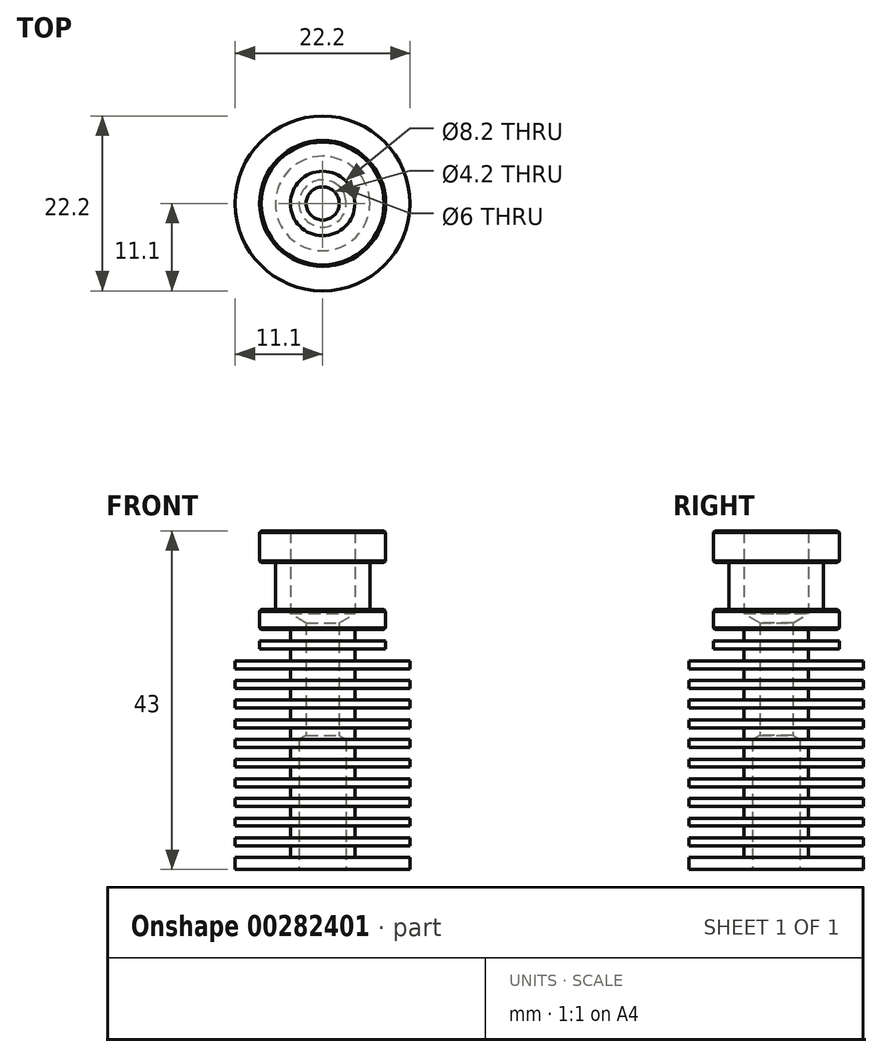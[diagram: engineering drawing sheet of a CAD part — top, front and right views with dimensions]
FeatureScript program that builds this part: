
annotation { "Feature Type Name" : "Feature", "Feature Type Description" : "" }
export const myFeature = defineFeature(function(context is Context, id is Id, definition is map)
    precondition{}
    {
        {
            var Q0;
            Q0=qCreatedBy(makeId("Front.planeOp"),FACE);
            var sketch = newSketch(context, id + "F0", { "sketchPlane" : qUnion([Q0])});
            skLineSegment(sketch, "E0", {"start": v(0, 0) * mm, "end": v(0, 43) * mm, "construction": true});
            skLineSegment(sketch, "E1", {"start": v(4.1, 43) * mm, "end": v(8, 43) * mm});
            skLineSegment(sketch, "E2", {"start": v(8, 43) * mm, "end": v(8, 39) * mm});
            skLineSegment(sketch, "E3", {"start": v(8, 39) * mm, "end": v(6, 39) * mm});
            skLineSegment(sketch, "E4", {"start": v(6, 39) * mm, "end": v(6, 33) * mm});
            skLineSegment(sketch, "E5", {"start": v(6, 33) * mm, "end": v(8, 33) * mm});
            skLineSegment(sketch, "E6", {"start": v(8, 33) * mm, "end": v(8, 30.5) * mm});
            skLineSegment(sketch, "E7", {"start": v(8, 30.5) * mm, "end": v(4.1, 30.5) * mm});
            skLineSegment(sketch, "E8", {"start": v(4.1, 30.5) * mm, "end": v(4.1, 29) * mm});
            skLineSegment(sketch, "E9", {"start": v(4.1, 29) * mm, "end": v(8, 29) * mm});
            skLineSegment(sketch, "E10", {"start": v(8, 29) * mm, "end": v(8, 28) * mm});
            skLineSegment(sketch, "E11", {"start": v(8, 28) * mm, "end": v(4.1, 28) * mm});
            skLineSegment(sketch, "E12", {"start": v(4.1, 28) * mm, "end": v(4.1, 26.5) * mm});
            skLineSegment(sketch, "E13", {"start": v(4.1, 26.5) * mm, "end": v(11.1, 26.5) * mm});
            skLineSegment(sketch, "E14", {"start": v(11.1, 26.5) * mm, "end": v(11.1, 25.5) * mm});
            skLineSegment(sketch, "E15", {"start": v(11.1, 25.5) * mm, "end": v(4.1, 25.5) * mm});
            skLineSegment(sketch, "E16", {"start": v(4.1, 25.5) * mm, "end": v(4.1, 24) * mm});
            skLineSegment(sketch, "E17", {"start": v(4.1, 24) * mm, "end": v(11.1, 24) * mm});
            skLineSegment(sketch, "E18", {"start": v(11.1, 24) * mm, "end": v(11.1, 23) * mm});
            skLineSegment(sketch, "E19", {"start": v(11.1, 23) * mm, "end": v(4.1, 23) * mm});
            skLineSegment(sketch, "E20", {"start": v(4.1, 23) * mm, "end": v(4.1, 21.5) * mm});
            skLineSegment(sketch, "E21", {"start": v(4.1, 21.5) * mm, "end": v(11.1, 21.5) * mm});
            skLineSegment(sketch, "E22", {"start": v(11.1, 21.5) * mm, "end": v(11.1, 20.5) * mm});
            skLineSegment(sketch, "E23", {"start": v(11.1, 20.5) * mm, "end": v(4.1, 20.5) * mm});
            skLineSegment(sketch, "E24", {"start": v(4.1, 20.5) * mm, "end": v(4.1, 19) * mm});
            skLineSegment(sketch, "E25", {"start": v(4.1, 19) * mm, "end": v(11.1, 19) * mm});
            skLineSegment(sketch, "E26", {"start": v(11.1, 19) * mm, "end": v(11.1, 18) * mm});
            skLineSegment(sketch, "E27", {"start": v(11.1, 18) * mm, "end": v(4.1, 18) * mm});
            skLineSegment(sketch, "E28", {"start": v(4.1, 18) * mm, "end": v(4.1, 16.5) * mm});
            skLineSegment(sketch, "E29", {"start": v(4.1, 16.5) * mm, "end": v(11.1, 16.5) * mm});
            skLineSegment(sketch, "E30", {"start": v(11.1, 16.5) * mm, "end": v(11.1, 15.5) * mm});
            skLineSegment(sketch, "E31", {"start": v(11.1, 15.5) * mm, "end": v(4.1, 15.5) * mm});
            skLineSegment(sketch, "E32", {"start": v(4.1, 15.5) * mm, "end": v(4.1, 14) * mm});
            skLineSegment(sketch, "E33", {"start": v(4.1, 14) * mm, "end": v(11.1, 14) * mm});
            skLineSegment(sketch, "E34", {"start": v(11.1, 14) * mm, "end": v(11.1, 13) * mm});
            skLineSegment(sketch, "E35", {"start": v(11.1, 13) * mm, "end": v(4.1, 13) * mm});
            skLineSegment(sketch, "E36", {"start": v(4.1, 13) * mm, "end": v(4.1, 11.5) * mm});
            skLineSegment(sketch, "E37", {"start": v(4.1, 11.5) * mm, "end": v(11.1, 11.5) * mm});
            skLineSegment(sketch, "E38", {"start": v(11.1, 11.5) * mm, "end": v(11.1, 10.5) * mm});
            skLineSegment(sketch, "E39", {"start": v(11.1, 10.5) * mm, "end": v(4.1, 10.5) * mm});
            skLineSegment(sketch, "E40", {"start": v(4.1, 10.5) * mm, "end": v(4.1, 9) * mm});
            skLineSegment(sketch, "E41", {"start": v(4.1, 9) * mm, "end": v(11.1, 9) * mm});
            skLineSegment(sketch, "E42", {"start": v(11.1, 9) * mm, "end": v(11.1, 8) * mm});
            skLineSegment(sketch, "E43", {"start": v(11.1, 8) * mm, "end": v(4.1, 8) * mm});
            skLineSegment(sketch, "E44", {"start": v(4.1, 8) * mm, "end": v(4.1, 6.5) * mm});
            skLineSegment(sketch, "E45", {"start": v(4.1, 6.5) * mm, "end": v(11.1, 6.5) * mm});
            skLineSegment(sketch, "E46", {"start": v(11.1, 6.5) * mm, "end": v(11.1, 5.5) * mm});
            skLineSegment(sketch, "E47", {"start": v(11.1, 5.5) * mm, "end": v(4.1, 5.5) * mm});
            skLineSegment(sketch, "E48", {"start": v(4.1, 5.5) * mm, "end": v(4.1, 4) * mm});
            skLineSegment(sketch, "E49", {"start": v(4.1, 4) * mm, "end": v(11.1, 4) * mm});
            skLineSegment(sketch, "E50", {"start": v(11.1, 4) * mm, "end": v(11.1, 3) * mm});
            skLineSegment(sketch, "E51", {"start": v(11.1, 3) * mm, "end": v(4.1, 3) * mm});
            skLineSegment(sketch, "E52", {"start": v(4.1, 3) * mm, "end": v(4.1, 1.5) * mm});
            skLineSegment(sketch, "E53", {"start": v(4.1, 1.5) * mm, "end": v(11.1, 1.5) * mm});
            skLineSegment(sketch, "E54", {"start": v(11.1, 1.5) * mm, "end": v(11.1, 0) * mm});
            skLineSegment(sketch, "E55", {"start": v(11.1, 0) * mm, "end": v(3, 0) * mm});
            skLineSegment(sketch, "E56", {"start": v(4.1, 43) * mm, "end": v(4.1, 32.5) * mm});
            skLineSegment(sketch, "E57", {"start": v(4.1, 32.5) * mm, "end": v(2.1, 31.3) * mm});
            skLineSegment(sketch, "E58", {"start": v(2.1, 31.3) * mm, "end": v(2.1, 17.04) * mm});
            skLineSegment(sketch, "E59", {"start": v(2.1, 17.04) * mm, "end": v(3, 16.5) * mm});
            skLineSegment(sketch, "E60", {"start": v(3, 16.5) * mm, "end": v(3, 0) * mm});
            skSolve(sketch);
        }
        {
            var Q0;
            Q0=qSketchRegion(id+"F0",true);
            var Q1;
            Q1=sQuery(id+"F0.wireOp",EDGE,"E0");
            revolve(context, id + "F1", {"entities" : qUnion([Q0]), "axis" : qUnion([Q1]), "revolveType" : RevolveType.FULL});
        }
        {
            var Q0;
            Q0=makeQuery(id+"F1.opRevolve","SWEPT_EDGE",EDGE,{"disambiguationData":[OSD([sQuery(id+"F0.wireOp",EDGE,"E6"),sQuery(id+"F0.wireOp",EDGE,"E7")])]});
            var Q1;
            Q1=makeQuery(id+"F1.opRevolve","SWEPT_EDGE",EDGE,{"disambiguationData":[OSD([sQuery(id+"F0.wireOp",EDGE,"E5"),sQuery(id+"F0.wireOp",EDGE,"E6")])]});
            var Q2;
            Q2=makeQuery(id+"F1.opRevolve","SWEPT_EDGE",EDGE,{"disambiguationData":[OSD([sQuery(id+"F0.wireOp",EDGE,"E2"),sQuery(id+"F0.wireOp",EDGE,"E3")])]});
            var Q3;
            Q3=makeQuery(id+"F1.opRevolve","SWEPT_EDGE",EDGE,{"disambiguationData":[OSD([sQuery(id+"F0.wireOp",EDGE,"E1"),sQuery(id+"F0.wireOp",EDGE,"E2")])]});
            chamfer(context, id + "F2", {"entities" : qUnion([Q0, Q1, Q2, Q3]), "width" : 0.2 * mm, "tangentPropagation" : true});
        }
    });
